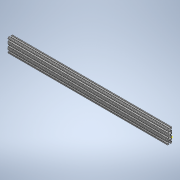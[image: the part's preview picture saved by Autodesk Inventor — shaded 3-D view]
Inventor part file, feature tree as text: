
AUTODESK INVENTOR PART (.ipt)
format: ipt  version: 2020 (Build 240168000, 168)  size: 393,216 bytes
history: native  units: in
note: dims shown in document units (in); Inventor stores cm internally (conversion verified against a paired STEP export)
features: sketch x2, extrude x1
ambient origin geometry x8: Origin, YZ Plane, XZ Plane, XY Plane, X Axis, Y Axis, Z Axis, Center Point
bodies: Solid1 (feature_tree)
feature tree (3):
  extrude  "Extrusion1"  [1 undecoded]
  sketch  "Sketch2"
  sketch  "Sketch1"  dims[d0=34.0in d1=0.0in]
note: 1 required parameter value undecoded (feature->parameter linkage not recoverable at this tier; creation-order binding heuristic only, values carry confidence <= 0.55)
